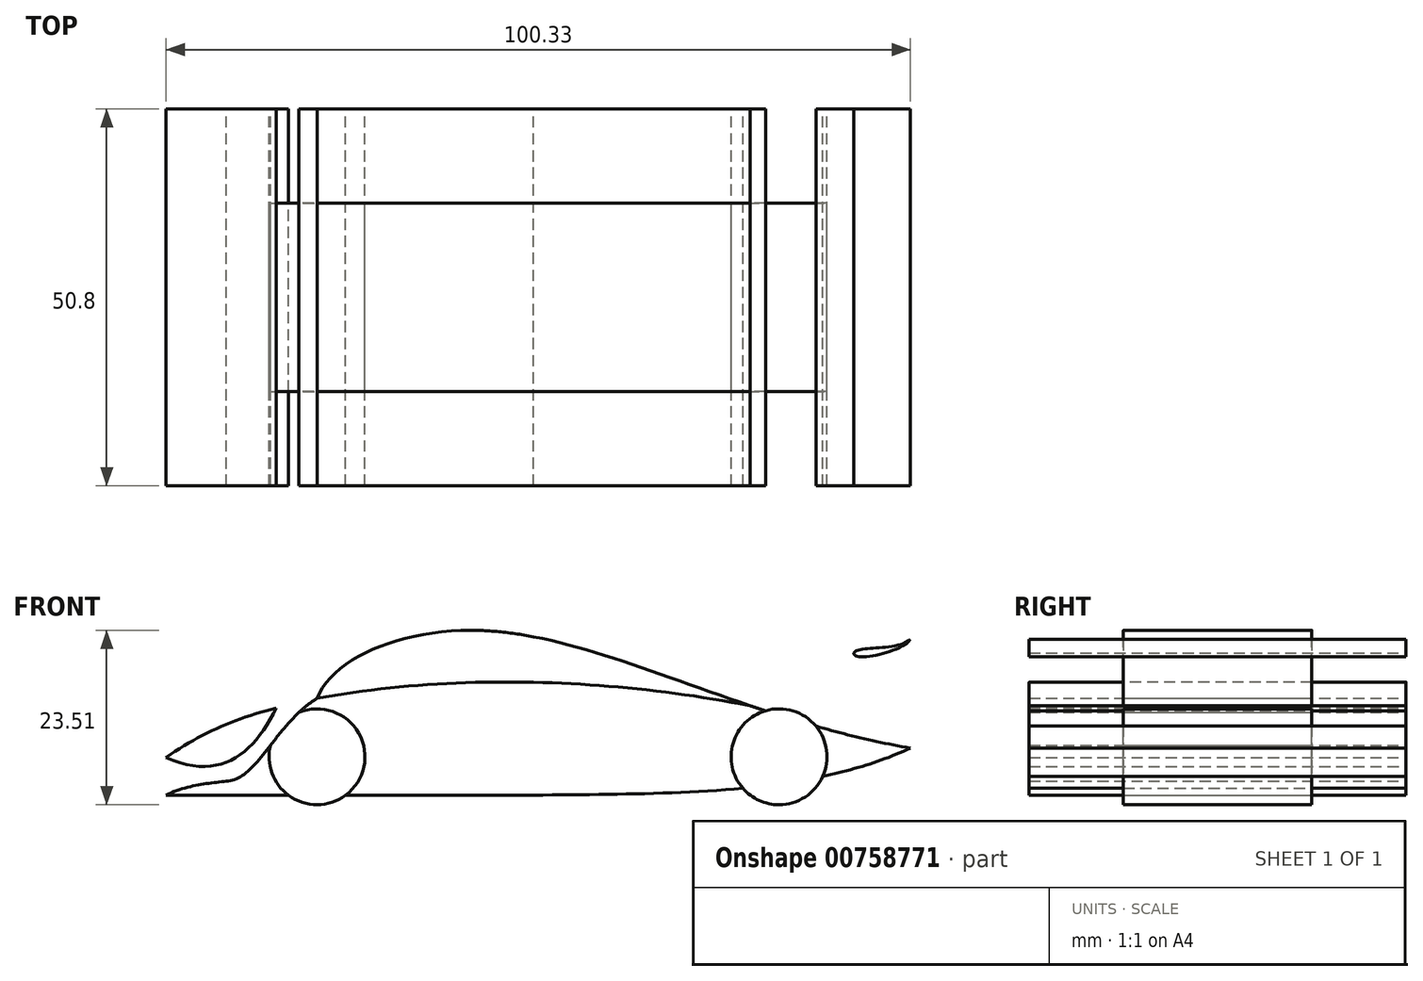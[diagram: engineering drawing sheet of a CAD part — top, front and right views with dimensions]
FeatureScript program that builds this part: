
annotation { "Feature Type Name" : "Feature", "Feature Type Description" : "" }
export const myFeature = defineFeature(function(context is Context, id is Id, definition is map)
    precondition{}
    {
        {
            var Q0;
            Q0=qCreatedBy(makeId("Front.planeOp"),FACE);
            var sketch = newSketch(context, id + "F0", { "sketchPlane" : qUnion([Q0])});
            skLineSegment(sketch, "E0", {"start": v(0, 0) * mm, "end": v(0, 30.48) * mm});
            skLineSegment(sketch, "E1", {"start": v(0, 0) * mm, "end": v(0, 1.27) * mm});
            skLineSegment(sketch, "E2", {"start": v(0, 1.27) * mm, "end": v(-50.8, 1.27) * mm});
            skFitSpline(sketch, "E3", {"points": [v(0, 1.27) * mm, v(50.8, 7.62) * mm], "startDerivative": vector(55.17, 0.88) * mm, "endDerivative": vector(43.03, 19.72) * mm});
            skLineSegment(sketch, "E4", {"start": v(-7.14, 23.48) * mm, "end": v(50.8, 23.48) * mm});
            skLineSegment(sketch, "E5", {"start": v(50.8, 23.48) * mm, "end": v(50.8, 7.62) * mm});
            skLineSegment(sketch, "E6", {"start": v(50.8, 23.48) * mm, "end": v(43.18, 23.48) * mm});
            skFitSpline(sketch, "E7", {"points": [v(43.18, 20.44) * mm, v(50.8, 22.29) * mm], "startDerivative": vector(1.18, 3.22) * mm, "endDerivative": vector(6.03, 5.07) * mm});
            skFitSpline(sketch, "E8", {"points": [v(43.18, 20.44) * mm, v(50.8, 22.29) * mm], "startDerivative": vector(-0.59, -3.76) * mm, "endDerivative": vector(4.19, 5.68) * mm});
            skFitSpline(sketch, "E9", {"points": [v(-49.53, 1.27) * mm, v(-41.44, 3.17) * mm], "startDerivative": vector(8.14, 4.16) * mm, "endDerivative": vector(7.23, 0.9) * mm});
            skFitSpline(sketch, "E10", {"points": [v(-49.53, 6.36) * mm, v(-34.7, 13.04) * mm], "startDerivative": vector(13.79, 9.74) * mm, "endDerivative": vector(16.5, 4.25) * mm});
            skFitSpline(sketch, "E11", {"points": [v(-29.18, 14.33) * mm, v(50.8, 7.62) * mm], "startDerivative": vector(74.75, 13.72) * mm, "endDerivative": vector(75.58, -25.82) * mm});
            skFitSpline(sketch, "E12", {"points": [v(-49.53, 6.36) * mm, v(-34.7, 13.04) * mm], "startDerivative": vector(22.32, -9.8) * mm, "endDerivative": vector(9.08, 18.55) * mm});
            skFitSpline(sketch, "E13", {"points": [v(-41.44, 3.17) * mm, v(-29.18, 14.33) * mm], "startDerivative": vector(12.42, 0.09) * mm, "endDerivative": vector(17.12, 10.55) * mm});
            skFitSpline(sketch, "E14", {"points": [v(-29.18, 14.33) * mm, v(-7.14, 23.48) * mm, v(50.8, 7.62) * mm], "startDerivative": vector(16.97, 43.78) * mm, "endDerivative": vector(117.45, -20.83) * mm});
            skCircle(sketch, "E15", {"center": v(-29.18, 6.46) * mm, "radius": 6.46 * mm});
            skCircle(sketch, "E16", {"center": v(33.09, 6.46) * mm, "radius": 6.46 * mm});
            skSolve(sketch);
        }
        {
            var Q0;
            {var subQ0=sQuery(id+"F0.wireOp",EDGE,"E11");var subQ1=sQuery(id+"F0.wireOp",EDGE,"E0");var subQ2=makeQuery(id+"F0.imprint","INTERSECT",VERTEX,{"derivedFrom":[subQ1,subQ0]});Q0=makeQuery(id+"F0.imprint","IMPRINT",FACE,{"disambiguationData":[TD([[makeQuery(id+"F0.imprint","IMPRINT",EDGE,{"disambiguationData":[TD([[subQ2,-1.0]])],"derivedFrom":subQ1}),1.0]])]});}
            var Q1;
            {var subQ0=sQuery(id+"F0.wireOp",EDGE,"E11");var subQ1=sQuery(id+"F0.wireOp",EDGE,"E0");var subQ2=makeQuery(id+"F0.imprint","INTERSECT",VERTEX,{"derivedFrom":[subQ1,subQ0]});Q1=makeQuery(id+"F0.imprint","IMPRINT",FACE,{"disambiguationData":[TD([[makeQuery(id+"F0.imprint","IMPRINT",EDGE,{"disambiguationData":[TD([[subQ2,-1.0]])],"derivedFrom":subQ1}),-1.0]])]});}
            extrude(context, id + "F1", {"entities" : qUnion([Q0, Q1]), "endBound" : BoundingType.SYMMETRIC, "depth" : 25.4 * mm, "offsetDistance" : 25.4 * mm});
        }
        {
            var Q0;
            Q0=makeQuery(id+"F0.imprint","IMPRINT",FACE,{"disambiguationData":[TD([[makeQuery(id+"F0.imprint","IMPRINT",EDGE,{"derivedFrom":sQuery(id+"F0.wireOp",EDGE,"E7")}),-1.0]])]});
            extrude(context, id + "F2", {"entities" : qUnion([Q0]), "endBound" : BoundingType.SYMMETRIC, "depth" : 50.8 * mm, "offsetDistance" : 25.4 * mm});
        }
        {
            var Q0;
            Q0=makeQuery(id+"F0.imprint","IMPRINT",FACE,{"disambiguationData":[TD([[makeQuery(id+"F0.imprint","IMPRINT",EDGE,{"derivedFrom":sQuery(id+"F0.wireOp",EDGE,"E10")}),-1.0]])]});
            var Q1;
            {var subQ6=sQuery(id+"F0.wireOp",EDGE,"E9");Q1=makeQuery(id+"F0.imprint","IMPRINT",FACE,{"disambiguationData":[TD([[makeQuery(id+"F0.imprint","IMPRINT",EDGE,{"derivedFrom":subQ6}),-1.0]])]});}
            var Q2;
            {var subQ0=sQuery(id+"F0.wireOp",EDGE,"E3");Q2=makeQuery(id+"F0.imprint","IMPRINT",FACE,{"disambiguationData":[TD([[makeQuery(id+"F0.imprint","IMPRINT",EDGE,{"derivedFrom":subQ0}),1.0]])]});}
            extrude(context, id + "F3", {"entities" : qUnion([Q0, Q1, Q2]), "operationType" : NewBodyOperationType.ADD, "endBound" : BoundingType.SYMMETRIC, "depth" : 50.8 * mm, "offsetDistance" : 25.4 * mm});
        }
        {
            var Q0;
            {var subQ0=sQuery(id+"F0.wireOp",EDGE,"E15");var subQ1=sQuery(id+"F0.wireOp",EDGE,"E2");var subQ2=makeQuery(id+"F0.imprint","INTERSECT",VERTEX,{"disambiguationData":[OD(0.0)],"derivedFrom":[subQ1,subQ0]});Q0=makeQuery(id+"F0.imprint","IMPRINT",FACE,{"disambiguationData":[TD([[makeQuery(id+"F0.imprint","IMPRINT",EDGE,{"disambiguationData":[TD([[subQ2,-1.0]])],"derivedFrom":subQ1}),-1.0]])]});}
            var Q1;
            {var subQ0=sQuery(id+"F0.wireOp",EDGE,"E15");var subQ1=sQuery(id+"F0.wireOp",EDGE,"E2");var subQ2=makeQuery(id+"F0.imprint","INTERSECT",VERTEX,{"disambiguationData":[OD(0.0)],"derivedFrom":[subQ1,subQ0]});Q1=makeQuery(id+"F0.imprint","IMPRINT",FACE,{"disambiguationData":[TD([[makeQuery(id+"F0.imprint","IMPRINT",EDGE,{"disambiguationData":[TD([[subQ2,-1.0]])],"derivedFrom":subQ1}),1.0]])]});}
            var Q2;
            {var subQ0=sQuery(id+"F0.wireOp",EDGE,"E16");var subQ1=sQuery(id+"F0.wireOp",EDGE,"E3");var subQ2=makeQuery(id+"F0.imprint","INTERSECT",VERTEX,{"disambiguationData":[OD(0.0)],"derivedFrom":[subQ1,subQ0]});Q2=makeQuery(id+"F0.imprint","IMPRINT",FACE,{"disambiguationData":[TD([[makeQuery(id+"F0.imprint","IMPRINT",EDGE,{"disambiguationData":[TD([[subQ2,-1.0]])],"derivedFrom":subQ1}),1.0]])]});}
            var Q3;
            {var subQ0=sQuery(id+"F0.wireOp",EDGE,"E16");var subQ1=sQuery(id+"F0.wireOp",EDGE,"E3");var subQ2=makeQuery(id+"F0.imprint","INTERSECT",VERTEX,{"disambiguationData":[OD(0.0)],"derivedFrom":[subQ1,subQ0]});Q3=makeQuery(id+"F0.imprint","IMPRINT",FACE,{"disambiguationData":[TD([[makeQuery(id+"F0.imprint","IMPRINT",EDGE,{"disambiguationData":[TD([[subQ2,-1.0]])],"derivedFrom":subQ1}),-1.0]])]});}
            var Q4;
            {var subQ0=sQuery(id+"F0.wireOp",EDGE,"E16");var subQ1=sQuery(id+"F0.wireOp",EDGE,"E11");var subQ2=makeQuery(id+"F0.imprint","INTERSECT",VERTEX,{"disambiguationData":[OD(0.0)],"derivedFrom":[subQ1,subQ0]});Q4=makeQuery(id+"F0.imprint","IMPRINT",FACE,{"disambiguationData":[TD([[makeQuery(id+"F0.imprint","IMPRINT",EDGE,{"disambiguationData":[TD([[subQ2,-1.0]])],"derivedFrom":subQ1}),1.0]])]});}
            var Q5;
            {var subQ0=sQuery(id+"F0.wireOp",EDGE,"E16");var subQ1=sQuery(id+"F0.wireOp",EDGE,"E11");var subQ2=makeQuery(id+"F0.imprint","INTERSECT",VERTEX,{"disambiguationData":[OD(0.0)],"derivedFrom":[subQ1,subQ0]});Q5=makeQuery(id+"F0.imprint","IMPRINT",FACE,{"disambiguationData":[TD([[makeQuery(id+"F0.imprint","IMPRINT",EDGE,{"disambiguationData":[TD([[subQ2,-1.0]])],"derivedFrom":subQ1}),-1.0]])]});}
            extrude(context, id + "F4", {"entities" : qUnion([Q0, Q1, Q2, Q3, Q4, Q5]), "endBound" : BoundingType.SYMMETRIC, "depth" : 25.4 * mm, "offsetDistance" : 25.4 * mm});
        }
        {
            var Q0;
            {var subQ3=sQuery(id+"F0.wireOp",EDGE,"E15");var subQ7=sQuery(id+"F0.wireOp",EDGE,"E2");var subQ9=makeQuery(id+"F0.imprint","INTERSECT",VERTEX,{"disambiguationData":[OD(0.0)],"derivedFrom":[subQ7,subQ3]});Q0=makeQuery(id+"F0.imprint","IMPRINT",FACE,{"disambiguationData":[TD([[makeQuery(id+"F0.imprint","IMPRINT",EDGE,{"disambiguationData":[TD([[subQ9,-1.0]])],"derivedFrom":subQ3}),-1.0]])]});}
            var Q1;
            {var subQ0=sQuery(id+"F0.wireOp",EDGE,"E11");var subQ1=sQuery(id+"F0.wireOp",EDGE,"E0");var subQ2=makeQuery(id+"F0.imprint","INTERSECT",VERTEX,{"derivedFrom":[subQ1,subQ0]});Q1=makeQuery(id+"F0.imprint","IMPRINT",FACE,{"disambiguationData":[TD([[makeQuery(id+"F0.imprint","IMPRINT",EDGE,{"disambiguationData":[TD([[subQ2,-1.0]])],"derivedFrom":subQ0}),-1.0]])]});}
            extrude(context, id + "F5", {"entities" : qUnion([Q0, Q1]), "endBound" : BoundingType.SYMMETRIC, "depth" : 50.8 * mm, "offsetDistance" : 25.4 * mm});
        }
    });
